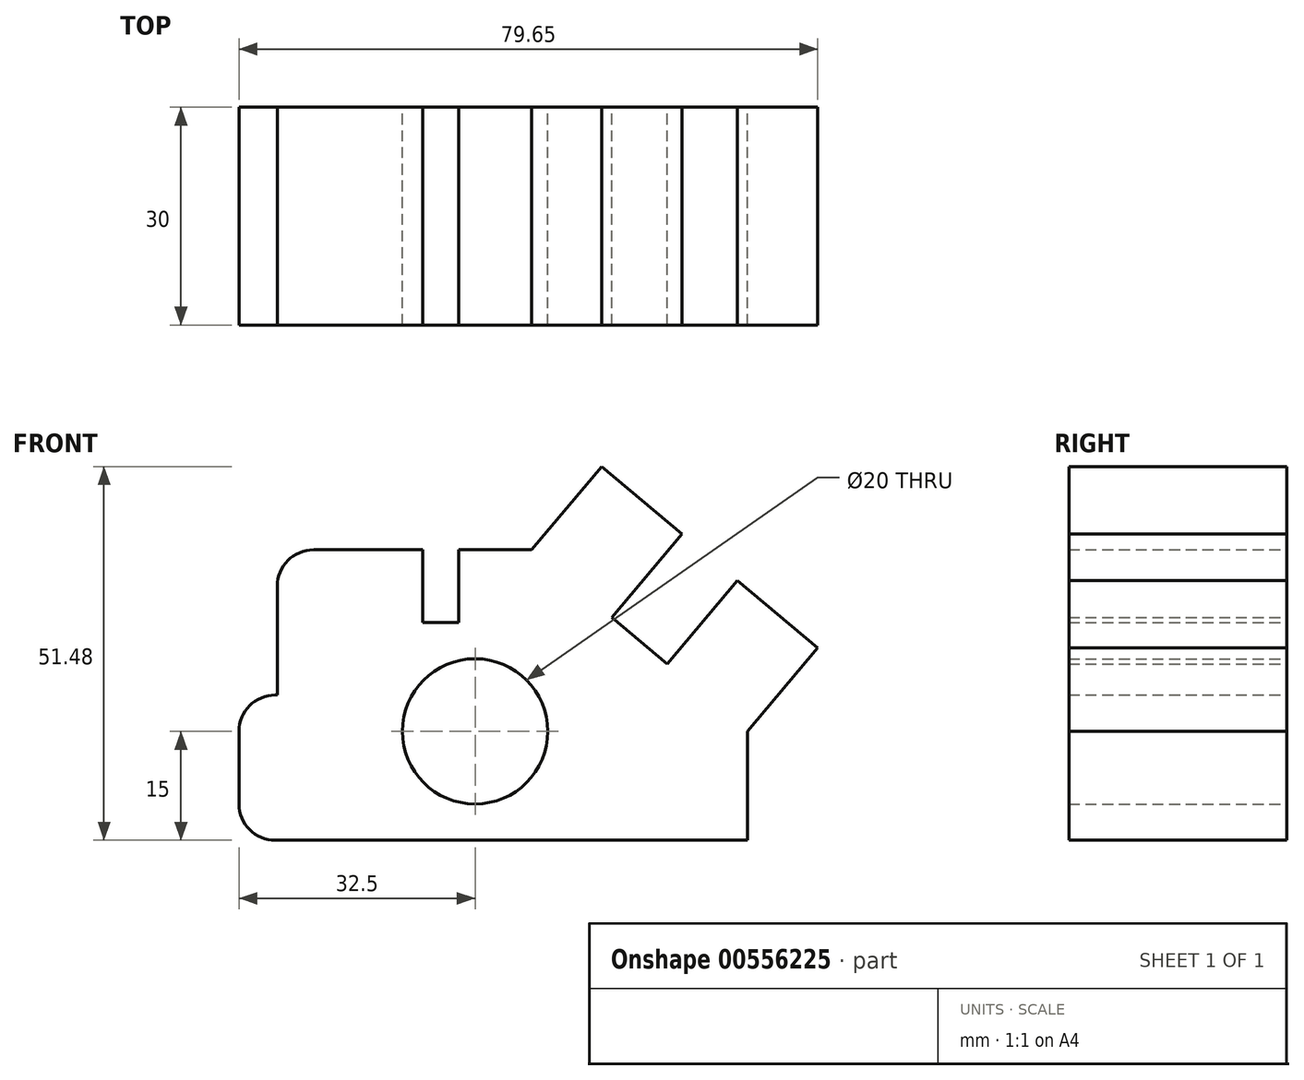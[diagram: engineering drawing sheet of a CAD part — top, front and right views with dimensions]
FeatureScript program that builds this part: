
annotation { "Feature Type Name" : "Feature", "Feature Type Description" : "" }
export const myFeature = defineFeature(function(context is Context, id is Id, definition is map)
    precondition{}
    {
        {
            var Q0;
            Q0=qCreatedBy(makeId("Front.planeOp"),FACE);
            var sketch = newSketch(context, id + "F0", { "sketchPlane" : qUnion([Q0])});
            skCircle(sketch, "E0", {"center": v(0, 0) * mm, "radius": 10 * mm});
            skLineSegment(sketch, "E1", {"start": v(-27.5, -15) * mm, "end": v(37.5, -15) * mm});
            skLineSegment(sketch, "E2", {"start": v(37.5, -15) * mm, "end": v(37.5, 0) * mm});
            skLineSegment(sketch, "E3", {"start": v(37.5, 0) * mm, "end": v(47.15, 11.48) * mm});
            skLineSegment(sketch, "E4", {"start": v(47.15, 11.48) * mm, "end": v(36.12, 20.76) * mm});
            skLineSegment(sketch, "E5", {"start": v(36.12, 20.76) * mm, "end": v(26.46, 9.28) * mm});
            skLineSegment(sketch, "E6", {"start": v(26.46, 9.28) * mm, "end": v(18.8, 15.72) * mm});
            skLineSegment(sketch, "E7", {"start": v(18.8, 15.72) * mm, "end": v(28.46, 27.2) * mm});
            skLineSegment(sketch, "E8", {"start": v(28.46, 27.2) * mm, "end": v(17.43, 36.48) * mm});
            skLineSegment(sketch, "E9", {"start": v(17.43, 36.48) * mm, "end": v(7.77, 25) * mm});
            skLineSegment(sketch, "E10", {"start": v(7.77, 25) * mm, "end": v(-2.23, 25) * mm});
            skLineSegment(sketch, "E11", {"start": v(-7.23, 25) * mm, "end": v(-22.23, 25) * mm});
            skLineSegment(sketch, "E12", {"start": v(-27.23, 20) * mm, "end": v(-27.23, 5) * mm});
            skLineSegment(sketch, "E13", {"start": v(-27.23, 5) * mm, "end": v(-27.5, 5) * mm});
            skLineSegment(sketch, "E14", {"start": v(-32.5, 0) * mm, "end": v(-32.5, -10) * mm});
            skLineSegment(sketch, "E15", {"start": v(-7.23, 25) * mm, "end": v(-7.23, 15) * mm});
            skLineSegment(sketch, "E16", {"start": v(-7.23, 15) * mm, "end": v(-2.23, 15) * mm});
            skLineSegment(sketch, "E17", {"start": v(-2.23, 15) * mm, "end": v(-2.23, 25) * mm});
            skPoint(sketch, "E18.visualSharp", {"position": v(-27.23, 25) * mm});
            skArc(sketch, "E18.filletArc", {"start": v(-22.23, 25) * mm, "mid": v(-25.76, 23.54) * mm, "end": v(-27.23, 20) * mm});
            skPoint(sketch, "E19.visualSharp", {"position": v(-32.5, 5) * mm});
            skArc(sketch, "E19.filletArc", {"start": v(-27.5, 5) * mm, "mid": v(-31.04, 3.54) * mm, "end": v(-32.5, 0) * mm});
            skPoint(sketch, "E20.visualSharp", {"position": v(-32.5, -15) * mm});
            skArc(sketch, "E20.filletArc", {"start": v(-32.5, -10) * mm, "mid": v(-31.04, -13.54) * mm, "end": v(-27.5, -15) * mm});
            skSolve(sketch);
        }
        {
            var Q0;
            Q0 = qSketchRegion(id + "F0", true);
            extrude(context, id + "F1", {"entities" : qUnion([Q0]), "depth" : 30 * mm, "offsetDistance" : 25 * mm});
        }
    });
